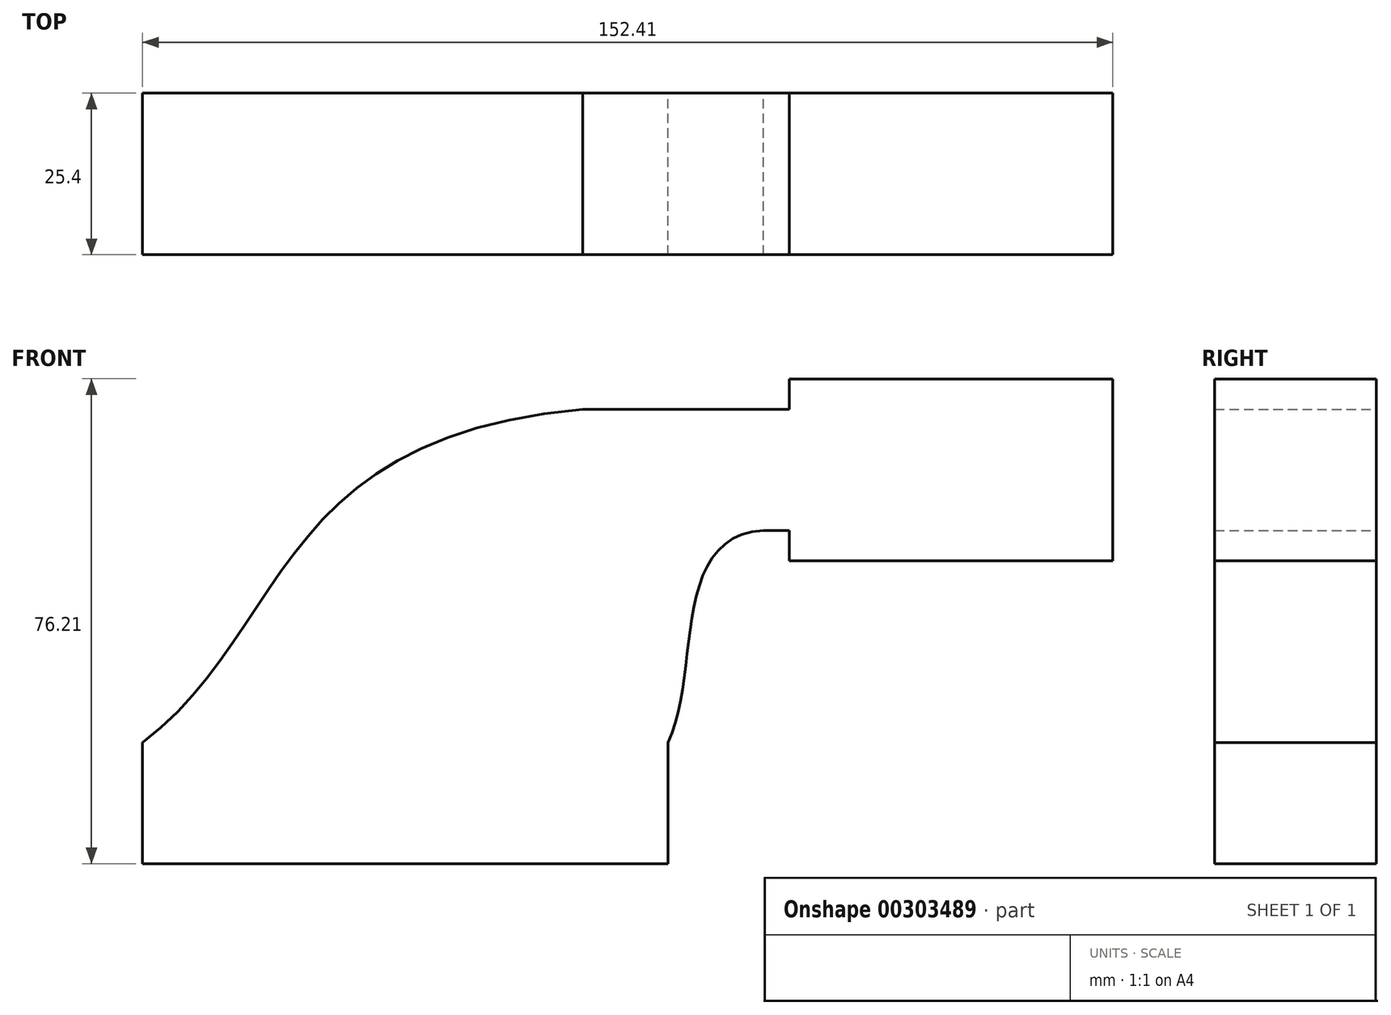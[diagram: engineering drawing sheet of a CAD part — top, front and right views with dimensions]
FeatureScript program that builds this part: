
annotation { "Feature Type Name" : "Feature", "Feature Type Description" : "" }
export const myFeature = defineFeature(function(context is Context, id is Id, definition is map)
    precondition{}
    {
        {
            var Q0;
            Q0=qCreatedBy(makeId("Front.planeOp"),FACE);
            var sketch = newSketch(context, id + "F0", { "sketchPlane" : qUnion([Q0])});
            skLineSegment(sketch, "E0.bottom", {"start": v(41.28, -9.52) * mm, "end": v(-41.28, -9.52) * mm});
            skLineSegment(sketch, "E0.top", {"start": v(41.28, 9.53) * mm, "end": v(-41.28, 9.53) * mm});
            skLineSegment(sketch, "E0.left", {"start": v(41.28, -9.52) * mm, "end": v(41.28, 9.53) * mm});
            skLineSegment(sketch, "E0.right", {"start": v(-41.28, -9.52) * mm, "end": v(-41.28, 9.53) * mm});
            skPoint(sketch, "E0.middle", {"position": v(0, 0) * mm});
            skLineSegment(sketch, "E1.bottom", {"start": v(111.12, 38.1) * mm, "end": v(60.32, 38.1) * mm});
            skLineSegment(sketch, "E1.top", {"start": v(111.12, 66.68) * mm, "end": v(60.32, 66.68) * mm});
            skLineSegment(sketch, "E1.left", {"start": v(111.12, 38.1) * mm, "end": v(111.12, 66.68) * mm});
            skLineSegment(sketch, "E1.right", {"start": v(60.32, 38.1) * mm, "end": v(60.32, 66.68) * mm});
            skPoint(sketch, "E1.middle", {"position": v(85.72, 52.39) * mm});
            skLineSegment(sketch, "E2", {"start": v(41.28, 9.53) * mm, "end": v(41.28, 42.88) * mm});
            skLineSegment(sketch, "E3", {"start": v(41.28, 42.85) * mm, "end": v(84.13, 42.85) * mm});
            skPoint(sketch, "E3.startSnap0", {"position": v(57.94, 42.85) * mm});
            skLineSegment(sketch, "E4.0", {"start": v(27.86, 61.9) * mm, "end": v(84.13, 61.9) * mm});
            skArc(sketch, "E4.1", {"start": v(22.22, 42.88) * mm, "mid": v(23.66, 52.8) * mm, "end": v(27.86, 61.9) * mm});
            skLineSegment(sketch, "E4.2", {"start": v(22.22, 9.53) * mm, "end": v(22.22, 42.88) * mm});
            skLineSegment(sketch, "E5", {"start": v(84.13, 61.9) * mm, "end": v(84.13, 42.85) * mm});
            skFitSpline(sketch, "E6", {"points": [v(-41.28, 9.52) * mm, v(27.86, 61.9) * mm], "startDerivative": vector(69.14, 52.37) * mm, "endDerivative": vector(146.5, 13.1) * mm});
            skFitSpline(sketch, "E7", {"points": [v(57.15, 42.88) * mm, v(41.28, 9.53) * mm], "startDerivative": vector(-47.62, -0.08) * mm, "endDerivative": vector(-15.87, -33.35) * mm});
            skSolve(sketch);
        }
        {
            var Q0;
            Q0 = qSketchRegion(id + "F0", true);
            extrude(context, id + "F1", {"entities" : qUnion([Q0]), "depth" : 25.4 * mm});
        }
    });
